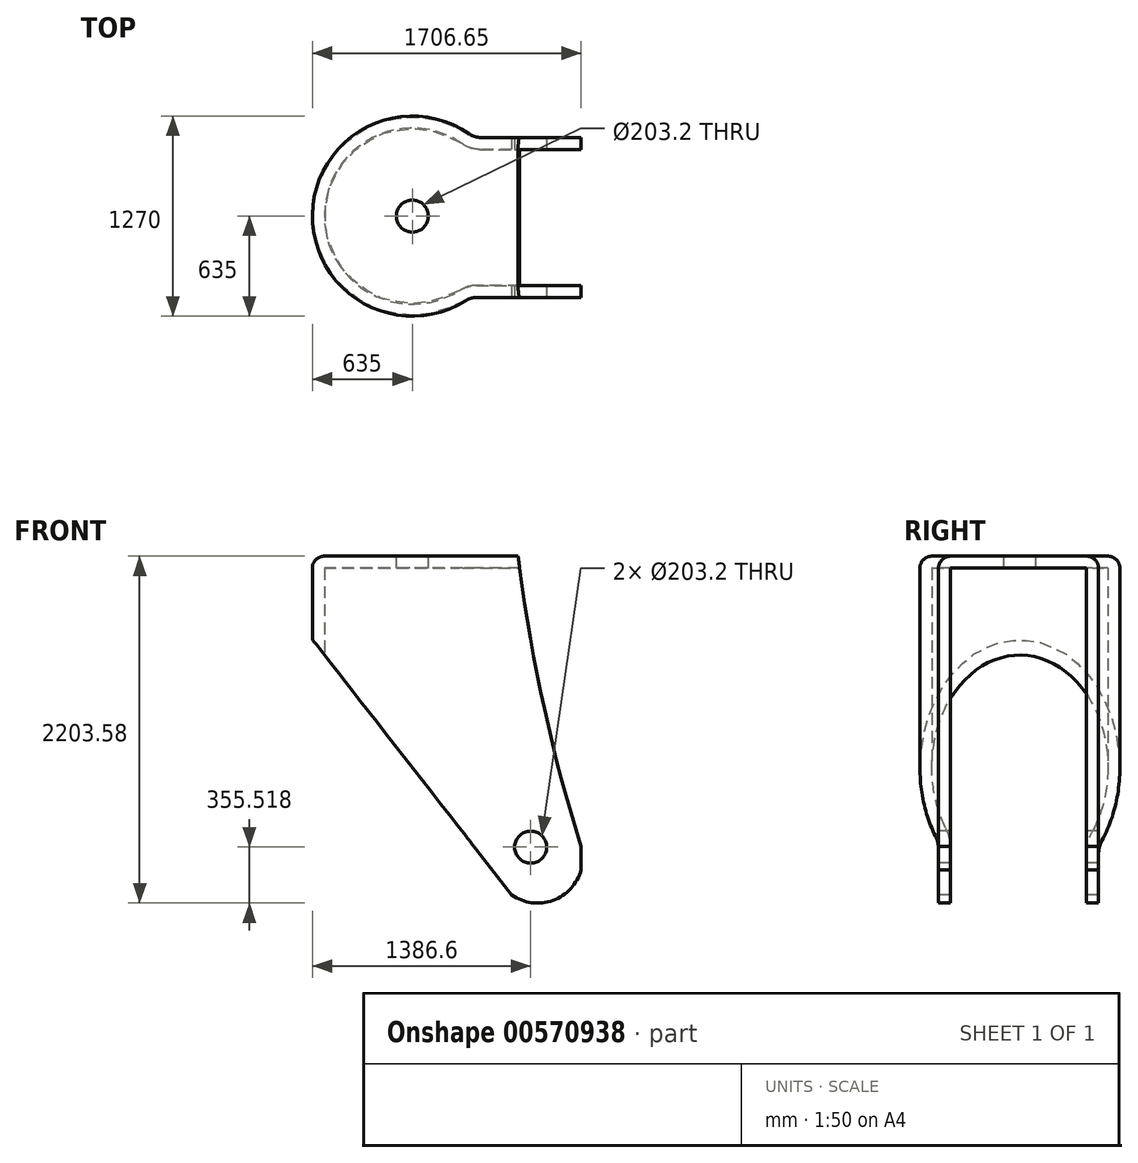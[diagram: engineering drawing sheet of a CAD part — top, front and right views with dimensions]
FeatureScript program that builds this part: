
annotation { "Feature Type Name" : "Feature", "Feature Type Description" : "" }
export const myFeature = defineFeature(function(context is Context, id is Id, definition is map)
    precondition{}
    {
        {
            var Q0;
            Q0=qCreatedBy(makeId("Top.planeOp"),FACE);
            var sketch = newSketch(context, id + "F0", { "sketchPlane" : qUnion([Q0])});
            skLineSegment(sketch, "E0", {"start": v(433.92, 499.38) * mm, "end": v(1071.65, 499.38) * mm});
            skLineSegment(sketch, "E1", {"start": v(1071.65, 499.38) * mm, "end": v(1071.65, -516.62) * mm});
            skLineSegment(sketch, "E2", {"start": v(1071.65, -516.62) * mm, "end": v(407.93, -516.62) * mm});
            skArc(sketch, "E3", {"start": v(361.6, 521.99) * mm, "mid": v(-634.87, 13) * mm, "end": v(339.94, -536.35) * mm});
            skPoint(sketch, "E4.visualSharp", {"position": v(107.58, -107.95) * mm});
            skPoint(sketch, "E5.visualSharp", {"position": v(392.22, 499.38) * mm});
            skLineSegment(sketch, "E6", {"start": v(-213.7, 0) * mm, "end": v(504.65, 0) * mm, "construction": true});
            skArc(sketch, "E7.filletArc", {"start": v(361.6, 521.99) * mm, "mid": v(396.04, 505.17) * mm, "end": v(433.92, 499.38) * mm});
            skPoint(sketch, "E8.visualSharp", {"position": v(369.23, -516.62) * mm});
            skArc(sketch, "E8.filletArc", {"start": v(407.93, -516.62) * mm, "mid": v(372.53, -521.65) * mm, "end": v(339.94, -536.35) * mm});
            skSolve(sketch);
        }
        {
            var Q0;
            Q0 = qSketchRegion(id + "F0", true);
            extrude(context, id + "F1", {"entities" : qUnion([Q0]), "depth" : 2286 * mm, "offsetDistance" : 25.4 * mm});
        }
        {
            var Q0;
            Q0=makeQuery(id+"F1.opExtrude","SWEPT_FACE",FACE,{"disambiguationData":[OSD([sQuery(id+"F0.wireOp",EDGE,"E2")])]});
            var sketch = newSketch(context, id + "F2", { "sketchPlane" : qUnion([Q0])});
            skCircle(sketch, "E9", {"center": v(194.68, 102.87) * mm, "radius": 38.1 * mm});
            skSolve(sketch);
        }
        {
            var Q0;
            Q0 = qSketchRegion(id + "F2", true);
            extrude(context, id + "F3", {"entities" : qUnion([Q0]), "operationType" : NewBodyOperationType.REMOVE, "oppositeDirection" : true, "depth" : 421.64 * mm, "offsetDistance" : 25.4 * mm});
        }
        {
            var Q0;
            Q0=makeQuery(id+"F1.opExtrude","SWEPT_FACE",FACE,{"disambiguationData":[OSD([sQuery(id+"F0.wireOp",EDGE,"E2")])]});
            var sketch = newSketch(context, id + "F4", { "sketchPlane" : qUnion([Q0])});
            skLineSegment(sketch, "E10", {"start": v(-936.23, 2142.3) * mm, "end": v(631.2, 134.58) * mm});
            skLineSegment(sketch, "E11", {"start": v(650.92, 2466.16) * mm, "end": v(1553.32, 2466.16) * mm});
            skLineSegment(sketch, "E12", {"start": v(1553.32, 2466.16) * mm, "end": v(1384.39, -211.18) * mm});
            skLineSegment(sketch, "E13", {"start": v(1384.39, -211.18) * mm, "end": v(-978.86, -155.48) * mm});
            skLineSegment(sketch, "E14", {"start": v(-978.86, -155.48) * mm, "end": v(-936.23, 2142.3) * mm});
            skArc(sketch, "E15", {"start": v(631.2, 134.58) * mm, "mid": v(958.84, 133.62) * mm, "end": v(1071.65, 441.22) * mm});
            skArc(sketch, "E16", {"start": v(650.92, 2466.16) * mm, "mid": v(811.43, 1443.34) * mm, "end": v(1071.65, 441.22) * mm});
            skSolve(sketch);
        }
        {
            var Q0;
            {var subQ6=sQuery(id+"F4.wireOp",EDGE,"E11");Q0=makeQuery(id+"F4.imprint","IMPRINT",FACE,{"disambiguationData":[TD([[makeQuery(id+"F4.imprint","IMPRINT",EDGE,{"derivedFrom":subQ6}),-1.0]])]});}
            var Q1;
            {var subQ0=sQuery(id+"F0.wireOp",EDGE,"E2");var subQ1=makeQuery(id+"F1.opExtrude","CAP_EDGE",EDGE,{"disambiguationData":[OSD([subQ0])],"isStart":true});Q1=makeQuery(id+"F4.imprint","IMPRINT",FACE,{"disambiguationData":[TD([[makeQuery(id+"F4.imprint","IMPRINT",EDGE,{"derivedFrom":subQ1}),-1.0]])]});}
            var Q2;
            {var subQ0=sQuery(id+"F4.wireOp",EDGE,"E16");var subQ1=sQuery(id+"F0.wireOp",EDGE,"E2");var subQ4=makeQuery(id+"F4qdaVqHj2dVyCj_2.opFillet","BLEND_EDGE",EDGE,{"blendedFrom":[makeQuery(id+"F1.opExtrude","CAP_EDGE",EDGE,{"disambiguationData":[OSD([subQ1])],"isStart":false}),makeQuery(id+"F1.opExtrude","SWEPT_FACE",FACE,{"disambiguationData":[OSD([subQ1])]})],"blendedInto":[makeQuery(id+"F1.opExtrude","SWEPT_FACE",FACE,{"disambiguationData":[OSD([subQ1])]})]});var subQ5=makeQuery(id+"F4.imprint","INTERSECT",VERTEX,{"derivedFrom":[subQ4,subQ0]});Q2=makeQuery(id+"F4.imprint","IMPRINT",FACE,{"disambiguationData":[TD([[makeQuery(id+"F4.imprint","IMPRINT",EDGE,{"disambiguationData":[TD([[subQ5,-1.0]])],"derivedFrom":subQ0}),1.0]])]});}
            extrude(context, id + "F5", {"entities" : qUnion([Q0, Q1, Q2]), "operationType" : NewBodyOperationType.REMOVE, "endBound" : BoundingType.SYMMETRIC, "oppositeDirection" : true, "depth" : 4074.16 * mm, "offsetDistance" : 25.4 * mm});
        }
        {
            var Q0;
            Q0=makeQuery(id+"F5.boolean.opBoolean","COPY",FACE,{"derivedFrom":makeQuery(id+"F5.opExtrude","SWEPT_FACE",FACE,{"disambiguationData":[OSD([sQuery(id+"F4.wireOp",EDGE,"E10")])]})});
            var Q1;
            Q1=makeQuery(id+"F5.boolean.opBoolean","COPY",FACE,{"derivedFrom":makeQuery(id+"F5.opExtrude","SWEPT_FACE",FACE,{"disambiguationData":[OSD([sQuery(id+"F4.wireOp",EDGE,"E15")])]})});
            var Q2;
            Q2=makeQuery(id+"F1.opExtrude","SWEPT_FACE",FACE,{"disambiguationData":[OSD([sQuery(id+"F0.wireOp",EDGE,"E1")])]});
            var Q3;
            Q3=makeQuery(id+"F5.boolean.opBoolean","COPY",FACE,{"derivedFrom":makeQuery(id+"F5.opExtrude","SWEPT_FACE",FACE,{"disambiguationData":[OSD([sQuery(id+"F4.wireOp",EDGE,"E16")])]})});
            shell(context, id + "F6", {"entities" : qUnion([Q0, Q1, Q2, Q3]), "thickness" : 76.2 * mm});
        }
        {
            var Q0;
            Q0=makeQuery(id+"F1.opExtrude","SWEPT_FACE",FACE,{"disambiguationData":[OSD([sQuery(id+"F0.wireOp",EDGE,"E2")])]});
            var sketch = newSketch(context, id + "F7", { "sketchPlane" : qUnion([Q0])});
            skCircle(sketch, "E17", {"center": v(751.6, 437.94) * mm, "radius": 101.6 * mm});
            skSolve(sketch);
        }
        {
            var Q0;
            Q0 = qSketchRegion(id + "F7", true);
            extrude(context, id + "F8", {"entities" : qUnion([Q0]), "operationType" : NewBodyOperationType.REMOVE, "oppositeDirection" : true, "depth" : 1582.42 * mm, "offsetDistance" : 25.4 * mm});
        }
        {
            var Q0;
            Q0=makeQuery(id+"F1.opExtrude","CAP_EDGE",EDGE,{"disambiguationData":[OSD([sQuery(id+"F0.wireOp",EDGE,"E3")])],"isStart":false});
            fillet(context, id + "F9", {"entities" : qUnion([Q0]), "radius" : 76.2 * mm, "tangentPropagation" : true, "allowEdgeOverflow" : false});
        }
        {
            var Q0;
            Q0=makeQuery(id+"F1.opExtrude","SWEPT_FACE",FACE,{"disambiguationData":[OSD([sQuery(id+"F0.wireOp",EDGE,"E2")])]});
            var sketch = newSketch(context, id + "F10", { "sketchPlane" : qUnion([Q0])});
            skCircle(sketch, "E18", {"center": v(751.6, 437.94) * mm, "radius": 98.12 * mm});
            skSolve(sketch);
        }
        {
            var Q0;
            Q0 = qSketchRegion(id + "F10", true);
            extrude(context, id + "F11", {"entities" : qUnion([Q0]), "depth" : 101.6 * mm, "offsetDistance" : 25.4 * mm});
        }
        {
            var Q0;
            Q0=makeQuery(id+"F11.opExtrude","CAP_FACE",FACE,{"disambiguationData":[OSD([sQuery(id+"F10.wireOp",EDGE,"E18")])],"isStart":true});
            extrude(context, id + "F12", {"entities" : qUnion([Q0]), "operationType" : NewBodyOperationType.ADD, "depth" : 1143 * mm, "offsetDistance" : 25.4 * mm});
        }
        {
            var Q0;
            Q0=makeQuery(id+"F11.opExtrude","SWEPT_BODY",BODY,{"disambiguationData":[OSD([sQuery(id+"F10.wireOp",EDGE,"E18")])]});
            deleteBodies(context, id + "F13", {"entities" : qUnion([Q0])});
        }
        {
            var Q0;
            Q0=makeQuery(id+"F1.opExtrude","CAP_FACE",FACE,{"disambiguationData":[OSD([sQuery(id+"F0.wireOp",EDGE,"E0"),sQuery(id+"F0.wireOp",EDGE,"E1"),sQuery(id+"F0.wireOp",EDGE,"E2"),sQuery(id+"F0.wireOp",EDGE,"E3"),sQuery(id+"F0.wireOp",EDGE,"E7.filletArc"),sQuery(id+"F0.wireOp",EDGE,"E8.filletArc")])],"isStart":false});
            var sketch = newSketch(context, id + "F14", { "sketchPlane" : qUnion([Q0])});
            skCircle(sketch, "E19", {"center": v(0, 0) * mm, "radius": 101.6 * mm});
            skSolve(sketch);
        }
        {
            var Q0;
            Q0 = qSketchRegion(id + "F14", true);
            extrude(context, id + "F15", {"entities" : qUnion([Q0]), "operationType" : NewBodyOperationType.REMOVE, "endBound" : BoundingType.THROUGH_ALL, "oppositeDirection" : true, "depth" : 25.4 * mm, "offsetDistance" : 25.4 * mm});
        }
    });
